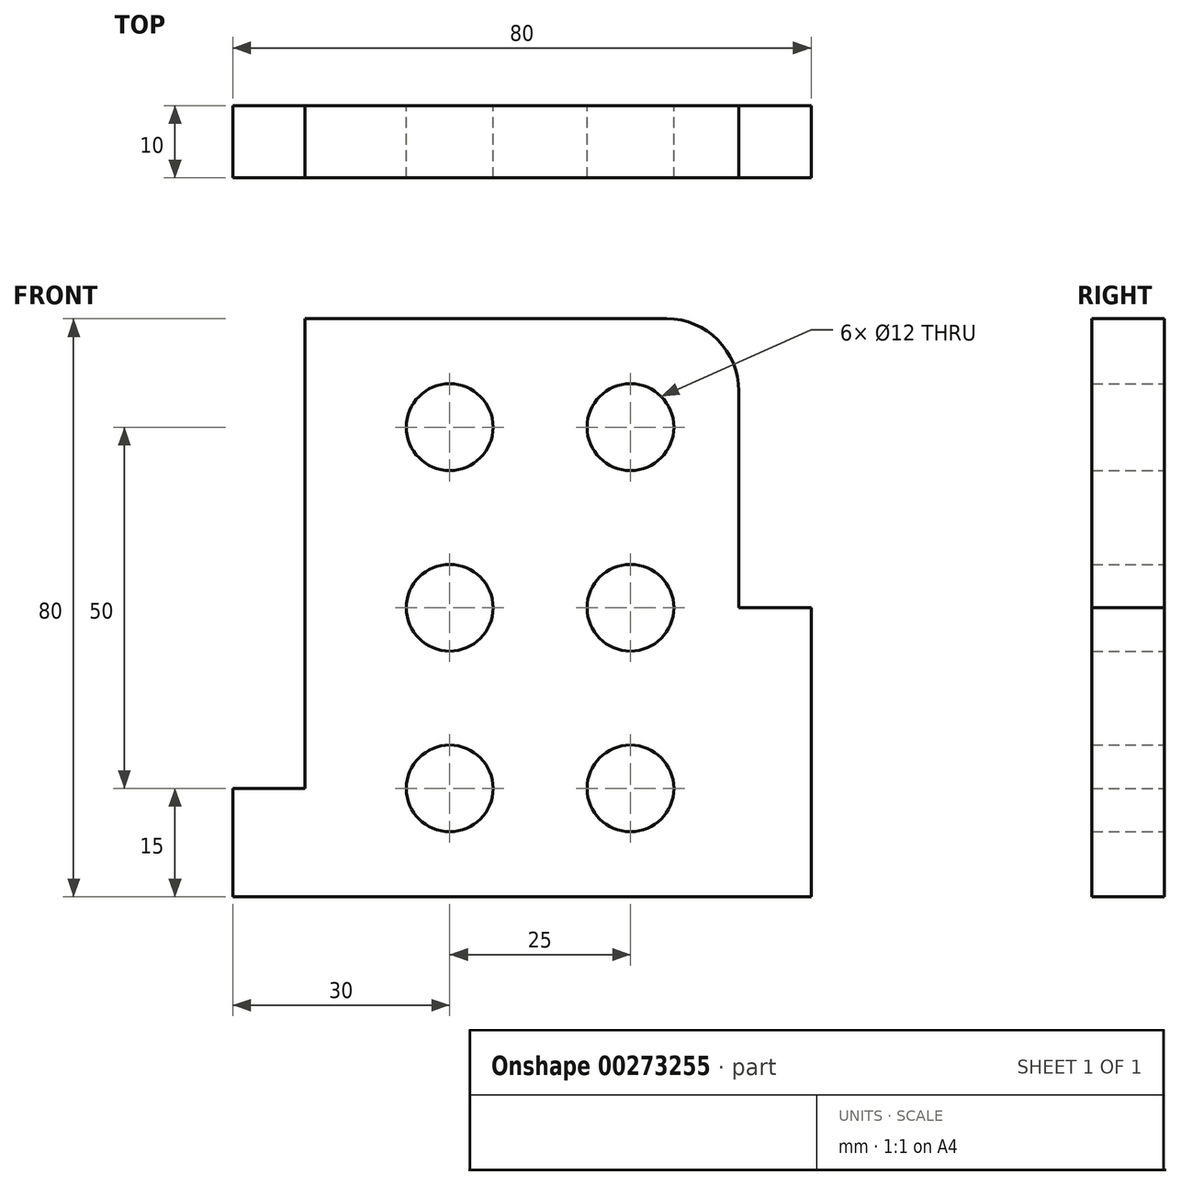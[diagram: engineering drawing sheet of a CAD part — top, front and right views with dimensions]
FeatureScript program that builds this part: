
annotation { "Feature Type Name" : "Feature", "Feature Type Description" : "" }
export const myFeature = defineFeature(function(context is Context, id is Id, definition is map)
    precondition{}
    {
        {
            var Q0;
            Q0=qCreatedBy(makeId("Front.planeOp"),FACE);
            var sketch = newSketch(context, id + "F0", { "sketchPlane" : qUnion([Q0])});
            skLineSegment(sketch, "E0", {"start": v(0, 0) * mm, "end": v(80, 0) * mm});
            skLineSegment(sketch, "E1", {"start": v(80, 0) * mm, "end": v(80, 40) * mm});
            skLineSegment(sketch, "E2", {"start": v(80, 40) * mm, "end": v(70, 40) * mm});
            skLineSegment(sketch, "E3", {"start": v(70, 40) * mm, "end": v(70, 70) * mm});
            skLineSegment(sketch, "E4", {"start": v(0, 0) * mm, "end": v(0, 15) * mm});
            skLineSegment(sketch, "E5", {"start": v(0, 15) * mm, "end": v(10, 15) * mm});
            skLineSegment(sketch, "E6", {"start": v(10, 15) * mm, "end": v(10, 80) * mm});
            skLineSegment(sketch, "E7", {"start": v(10, 80) * mm, "end": v(60, 80) * mm});
            skCircle(sketch, "E8", {"center": v(30, 15) * mm, "radius": 6 * mm});
            skCircle(sketch, "E9", {"center": v(55, 15) * mm, "radius": 6 * mm});
            skCircle(sketch, "E10", {"center": v(30, 40) * mm, "radius": 6 * mm});
            skCircle(sketch, "E11", {"center": v(55, 40) * mm, "radius": 6 * mm});
            skCircle(sketch, "E12", {"center": v(30, 65) * mm, "radius": 6 * mm});
            skCircle(sketch, "E13", {"center": v(55, 65) * mm, "radius": 6 * mm});
            skArc(sketch, "E14", {"start": v(60, 80) * mm, "mid": v(67.07, 77.07) * mm, "end": v(70, 70) * mm});
            skSolve(sketch);
        }
        {
            var Q0;
            Q0 = qSketchRegion(id + "F0", true);
            extrude(context, id + "F1", {"entities" : qUnion([Q0]), "depth" : 10 * mm});
        }
    });
